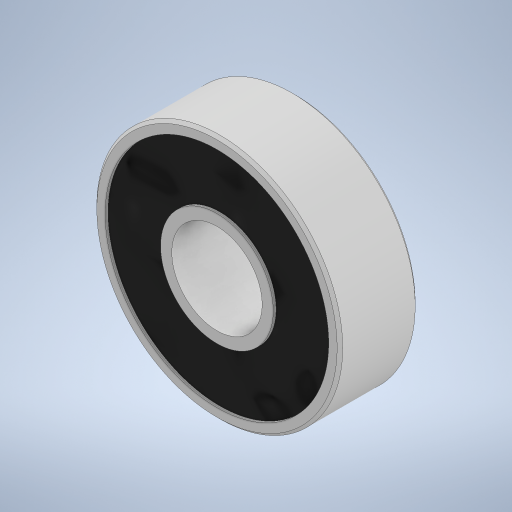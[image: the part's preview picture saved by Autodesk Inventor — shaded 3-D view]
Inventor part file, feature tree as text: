
AUTODESK INVENTOR PART (.ipt)
format: ipt  version: 2023 (Build 270158000, 158)  size: 268,288 bytes
history: native  units: mm
features: extrude x3, sketch x3, chamfer x1
ambient origin geometry x8: Origin, YZ Plane, XZ Plane, XY Plane, X Axis, Y Axis, Z Axis, Center Point
bodies: Solid1 (feature_tree)
feature tree (7):
  extrude  "Extrusion1"  Depth=8.1mm
  extrude  "Extrusion2"  Depth=7.0mm
  extrude  "Extrusion3"  Depth=0.25mm TaperAngle=0.0deg
  chamfer  "Chamfer1"  Distance=0.25mm
  sketch  "Sketch1"  dims[d0=22.05mm d1=8.1mm]
  sketch  "Sketch2"  dims[d2=7.0mm d3=0.0mm d4=1.0mm]
  sketch  "Sketch3"  dims[d5=1.0mm d6=0.25mm d7=0.0mm d8=0.25mm d9=0.0mm d10=0.25mm d11=2.0mm d12=45.0deg]
